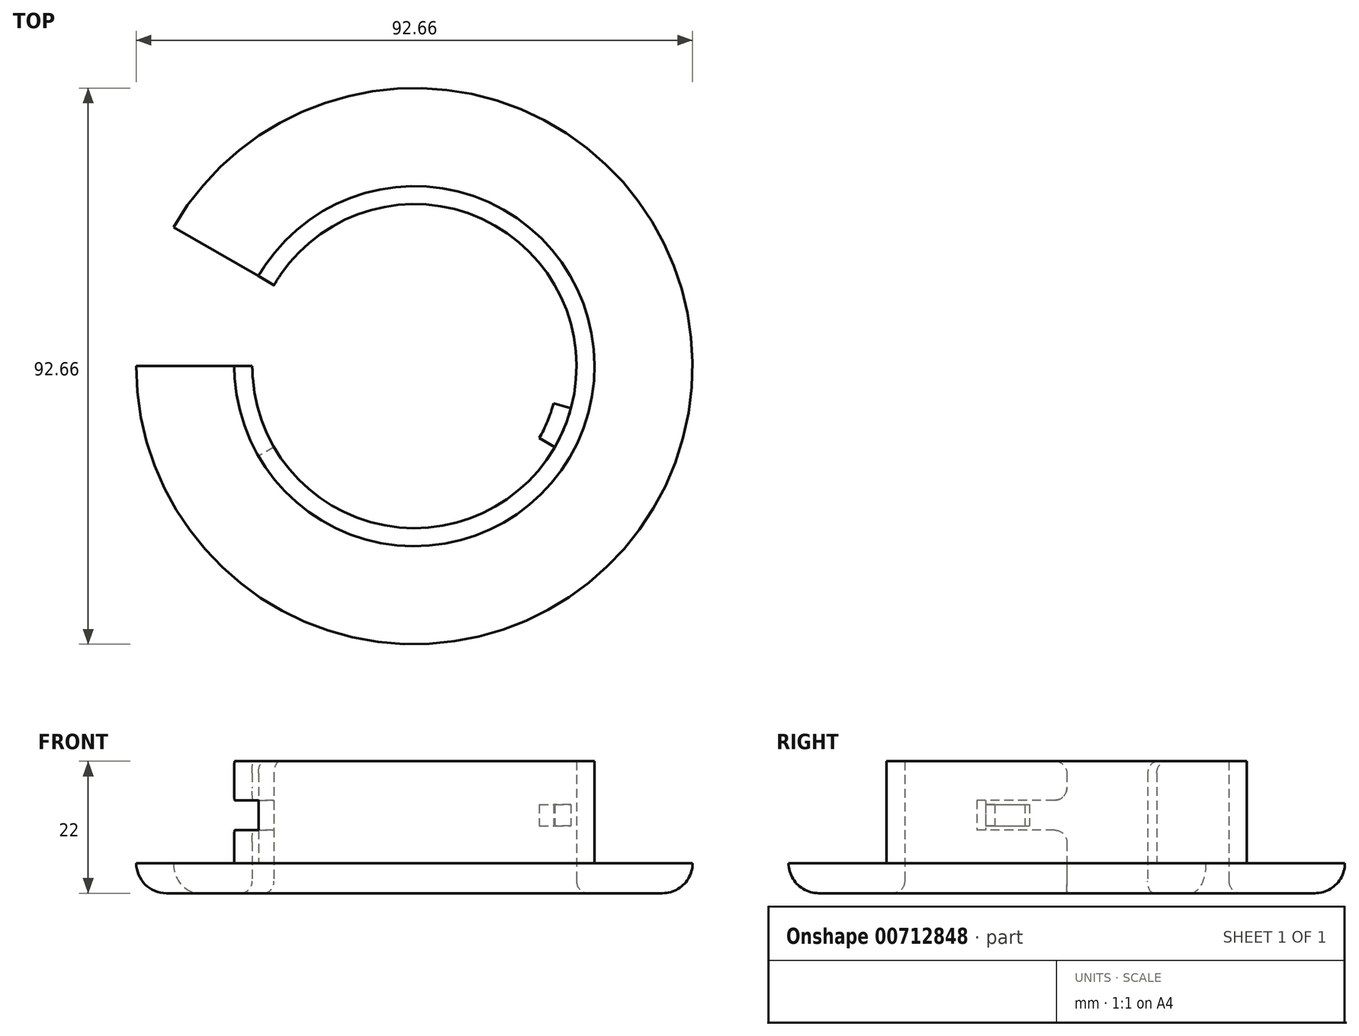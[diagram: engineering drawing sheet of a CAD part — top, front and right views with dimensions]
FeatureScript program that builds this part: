
annotation { "Feature Type Name" : "Feature", "Feature Type Description" : "" }
export const myFeature = defineFeature(function(context is Context, id is Id, definition is map)
    precondition{}
    {
        {
            var Q0;
            Q0=qCreatedBy(makeId("Front.planeOp"),FACE);
            var sketch = newSketch(context, id + "F0", { "sketchPlane" : qUnion([Q0])});
            skLineSegment(sketch, "E0", {"start": v(-30, 17) * mm, "end": v(-30, 0) * mm});
            skLineSegment(sketch, "E1", {"start": v(-30, 0) * mm, "end": v(-46.33, 0) * mm});
            skLineSegment(sketch, "E2", {"start": v(-46.33, 0) * mm, "end": v(-46.33, 0) * mm});
            skLineSegment(sketch, "E3", {"start": v(-41.33, -5) * mm, "end": v(-29, -5) * mm});
            skLineSegment(sketch, "E4", {"start": v(-27, -3) * mm, "end": v(-27, 17) * mm});
            skLineSegment(sketch, "E5", {"start": v(-27, 17) * mm, "end": v(-30, 17) * mm});
            skPoint(sketch, "E6.visualSharp", {"position": v(-46.33, -5) * mm});
            skArc(sketch, "E6.filletArc", {"start": v(-46.33, 0) * mm, "mid": v(-44.86, -3.54) * mm, "end": v(-41.33, -5) * mm});
            skPoint(sketch, "E7.visualSharp", {"position": v(-27, -5) * mm});
            skArc(sketch, "E7.filletArc", {"start": v(-29, -5) * mm, "mid": v(-27.59, -4.41) * mm, "end": v(-27, -3) * mm});
            skLineSegment(sketch, "E8", {"start": v(-30, 0) * mm, "end": v(0, 0) * mm, "construction": true});
            skLineSegment(sketch, "E9", {"start": v(0, 0) * mm, "end": v(0, 14.6) * mm, "construction": true});
            skSolve(sketch);
        }
        {
            var Q0;
            Q0=makeQuery(id+"F0.imprint","IMPRINT",FACE,{"disambiguationData":[TD([[makeQuery(id+"F0.imprint","IMPRINT",EDGE,{"derivedFrom":sQuery(id+"F0.wireOp",EDGE,"E0")}),1.0]])]});
            var Q1;
            Q1=sQuery(id+"F0.wireOp",EDGE,"E9");
            revolve(context, id + "F1", {"surfaceOperationType" : NewSurfaceOperationType.NEW, "entities" : qUnion([Q0]), "axis" : qUnion([Q1]), "revolveType" : RevolveType.FULL});
        }
        {
            var Q0;
            Q0=qCreatedBy(makeId("Top.planeOp"),FACE);
            var sketch = newSketch(context, id + "F2", { "sketchPlane" : qUnion([Q0])});
            skLineSegment(sketch, "E10", {"start": v(0, 0) * mm, "end": v(55.2, 0) * mm});
            skLineSegment(sketch, "E11", {"start": v(0, 0) * mm, "end": v(55.2, -31.87) * mm});
            skLineSegment(sketch, "E12", {"start": v(55.2, 0) * mm, "end": v(55.2, -31.87) * mm});
            skPoint(sketch, "E13", {"position": v(40.12, -23.16) * mm});
            skSolve(sketch);
        }
        {
            var Q0;
            Q0 = qSketchRegion(id + "F2", true);
            extrude(context, id + "F3", {"entities" : qUnion([Q0]), "operationType" : NewBodyOperationType.REMOVE, "endBound" : BoundingType.THROUGH_ALL, "depth" : 25 * mm, "offsetDistance" : 25 * mm, "hasSecondDirection" : true, "secondDirectionOppositeDirection" : true, "secondDirectionDepth" : 25 * mm});
        }
        {
            var Q0;
            Q0=qCreatedBy(makeId("Top.planeOp"),FACE);
            cPlane(context, id + "F4", {"entities" : qUnion([Q0]), "cplaneType" : CPlaneType.OFFSET, "offset" : 8 * mm, "width" : 150 * mm, "height" : 150 * mm});
        }
        {
            var Q0;
            Q0=makeQuery(id+"F1.opRevolve","SWEPT_BODY",BODY,{"disambiguationData":[OSD([sQuery(id+"F0.wireOp",EDGE,"E0"),sQuery(id+"F0.wireOp",EDGE,"E1"),sQuery(id+"F0.wireOp",EDGE,"E3"),sQuery(id+"F0.wireOp",EDGE,"E4"),sQuery(id+"F0.wireOp",EDGE,"E5"),sQuery(id+"F0.wireOp",EDGE,"E6.filletArc"),sQuery(id+"F0.wireOp",EDGE,"E7.filletArc")])]});
            var Q1;
            Q1=makeQuery(id+"F1.opRevolve","SWEPT_FACE",FACE,{"disambiguationData":[OSD([sQuery(id+"F0.wireOp",EDGE,"E0")])]});
            transform(context, id + "F5", {"entities" : qUnion([Q0]), "transformType" : TransformType.ROTATION, "transformAxis" : qUnion([Q1]), "angle" : 180 * degree, "oppositeDirection" : true, "makeCopy" : false});
        }
        {
            var Q0;
            Q0=qCreatedBy(id+"F4.planeOp",FACE);
            var sketch = newSketch(context, id + "F6", { "sketchPlane" : qUnion([Q0])});
            skPoint(sketch, "E14", {"position": v(0, 0) * mm});
            skLineSegment(sketch, "E15", {"start": v(0, 0) * mm, "end": v(37.46, 0) * mm, "construction": true});
            skLineSegment(sketch, "E16", {"start": v(0, 0) * mm, "end": v(-48.82, 0) * mm, "construction": true});
            skLineSegment(sketch, "E17", {"start": v(-18.24, 0) * mm, "end": v(0, 0) * mm});
            skLineSegment(sketch, "E18", {"start": v(26, -15.01) * mm, "end": v(25.98, -15) * mm});
            skLineSegment(sketch, "E19", {"start": v(0, 0) * mm, "end": v(26, -15.01) * mm, "construction": true});
            skLineSegment(sketch, "E20", {"start": v(0, 0) * mm, "end": v(29.5, -7.9) * mm, "construction": true});
            skPoint(sketch, "E21", {"position": v(23.38, -13.5) * mm});
            skPoint(sketch, "E22", {"position": v(20.78, -12) * mm});
            skArc(sketch, "E23", {"start": v(20.78, -12) * mm, "mid": v(22.17, -9.18) * mm, "end": v(23.18, -6.21) * mm});
            skLineSegment(sketch, "E24", {"start": v(20.78, -12) * mm, "end": v(24.06, -13.89) * mm});
            skLineSegment(sketch, "E25", {"start": v(24.06, -13.89) * mm, "end": v(26.82, -7.19) * mm});
            skLineSegment(sketch, "E26", {"start": v(26.82, -7.19) * mm, "end": v(23.18, -6.21) * mm});
            skLineSegment(sketch, "E27", {"start": v(0, 0) * mm, "end": v(-44.15, -25.49) * mm, "construction": true});
            skLineSegment(sketch, "E28", {"start": v(0, 0) * mm, "end": v(-34.13, -19.7) * mm});
            skLineSegment(sketch, "E29", {"start": v(-34.13, -19.7) * mm, "end": v(-34.9, 6.32) * mm});
            skLineSegment(sketch, "E30", {"start": v(-34.9, 6.32) * mm, "end": v(0, 0) * mm});
            skSolve(sketch);
        }
        {
            var Q0;
            Q0=makeQuery(id+"F6.imprint","IMPRINT",FACE,{"disambiguationData":[TD([[makeQuery(id+"F6.imprint","IMPRINT",EDGE,{"derivedFrom":sQuery(id+"F6.wireOp",EDGE,"E23")}),-1.0]])]});
            extrude(context, id + "F7", {"entities" : qUnion([Q0]), "operationType" : NewBodyOperationType.ADD, "endBound" : BoundingType.SYMMETRIC, "depth" : 3.6 * mm, "offsetDistance" : 25 * mm});
        }
        {
            var Q0;
            Q0=makeQuery(id+"F6.imprint","IMPRINT",FACE,{"disambiguationData":[TD([[makeQuery(id+"F6.imprint","IMPRINT",EDGE,{"derivedFrom":sQuery(id+"F6.wireOp",EDGE,"E28")}),-1.0]])]});
            extrude(context, id + "F8", {"entities" : qUnion([Q0]), "operationType" : NewBodyOperationType.REMOVE, "endBound" : BoundingType.SYMMETRIC, "oppositeDirection" : true, "depth" : 5 * mm, "offsetDistance" : 25 * mm});
        }
        {
            var Q0;
            Q0=makeQuery(id+"F8.boolean.opBoolean","INTERSECT",EDGE,{"derivedFrom":[makeQuery(id+"F3.boolean.opBoolean","COPY",FACE,{"derivedFrom":makeQuery(id+"F3.opExtrude","SWEPT_FACE",FACE,{"disambiguationData":[OSD([sQuery(id+"F2.wireOp",EDGE,"E10")])]})}),makeQuery(id+"F8.opExtrude","CAP_FACE",FACE,{"disambiguationData":[OSD([sQuery(id+"F6.wireOp",EDGE,"E28"),sQuery(id+"F6.wireOp",EDGE,"E29"),sQuery(id+"F6.wireOp",EDGE,"E30")])],"isStart":false})]});
            var Q1;
            Q1=makeQuery(id+"F8.boolean.opBoolean","INTERSECT",EDGE,{"derivedFrom":[makeQuery(id+"F3.boolean.opBoolean","COPY",FACE,{"derivedFrom":makeQuery(id+"F3.opExtrude","SWEPT_FACE",FACE,{"disambiguationData":[OSD([sQuery(id+"F2.wireOp",EDGE,"E10")])]})}),makeQuery(id+"F8.opExtrude","CAP_FACE",FACE,{"disambiguationData":[OSD([sQuery(id+"F6.wireOp",EDGE,"E28"),sQuery(id+"F6.wireOp",EDGE,"E29"),sQuery(id+"F6.wireOp",EDGE,"E30")])],"isStart":true})]});
            var Q2;
            Q2=makeQuery(id+"F3.boolean.opBoolean","INTERSECT",EDGE,{"derivedFrom":[makeQuery(id+"F1.opRevolve","SWEPT_FACE",FACE,{"disambiguationData":[OSD([sQuery(id+"F0.wireOp",EDGE,"E5")])]}),makeQuery(id+"F3.opExtrude","SWEPT_FACE",FACE,{"disambiguationData":[OSD([sQuery(id+"F2.wireOp",EDGE,"E10")])]})]});
            var Q3;
            Q3=makeQuery(id+"F3.boolean.opBoolean","INTERSECT",EDGE,{"derivedFrom":[makeQuery(id+"F1.opRevolve","SWEPT_FACE",FACE,{"disambiguationData":[OSD([sQuery(id+"F0.wireOp",EDGE,"E5")])]}),makeQuery(id+"F3.opExtrude","SWEPT_FACE",FACE,{"disambiguationData":[OSD([sQuery(id+"F2.wireOp",EDGE,"E11")])]})]});
            fillet(context, id + "F9", {"entities" : qUnion([Q0, Q1, Q2, Q3]), "radius" : 2 * mm, "tangentPropagation" : true, "allowEdgeOverflow" : false});
        }
    });
